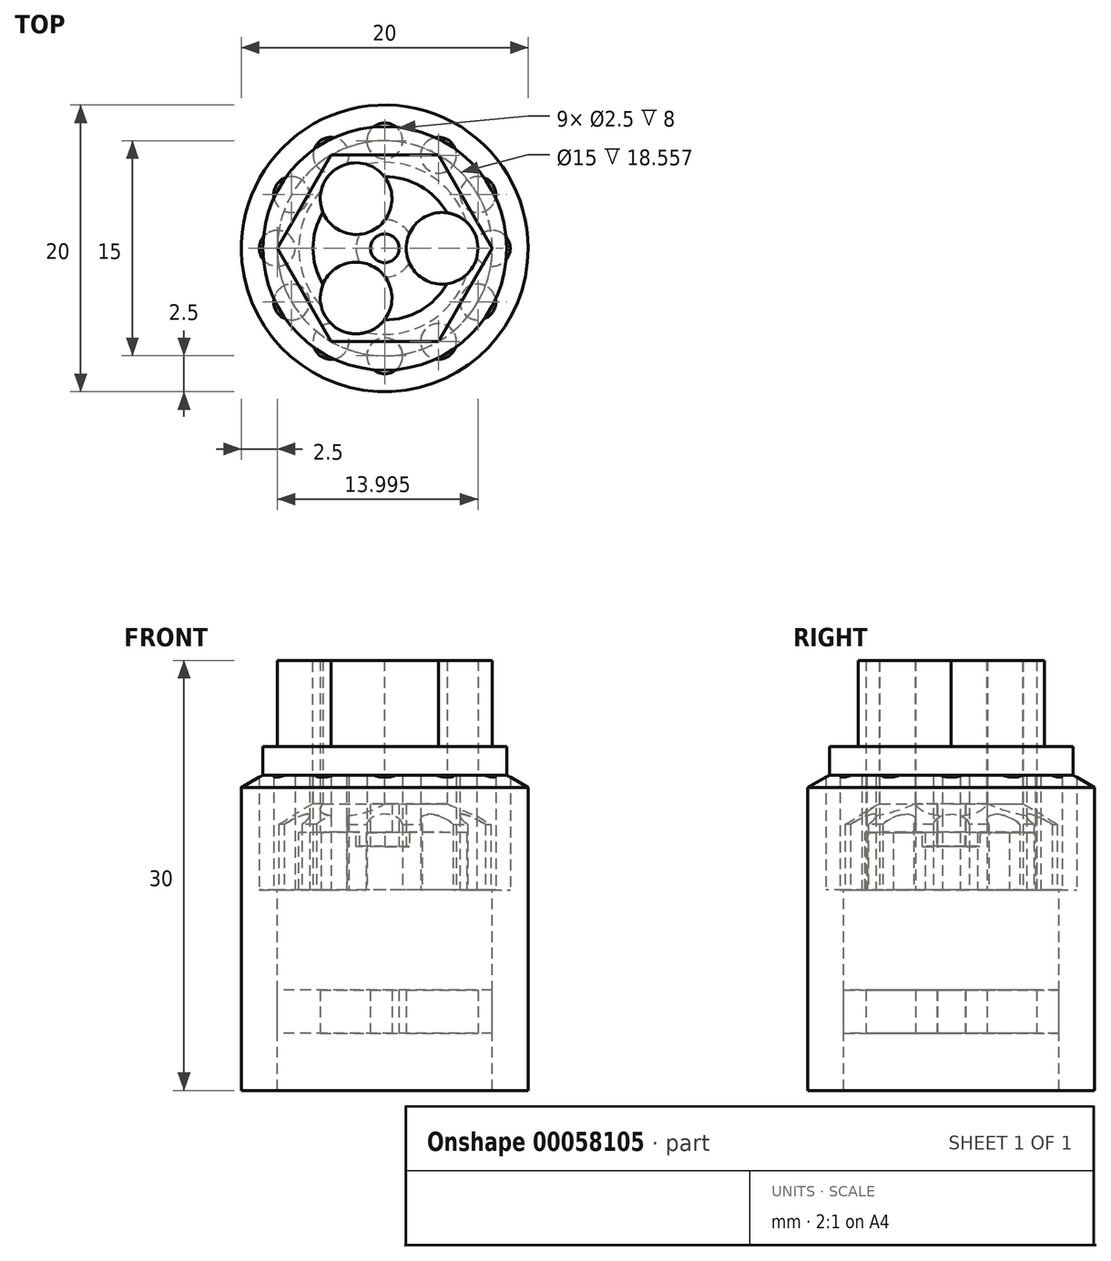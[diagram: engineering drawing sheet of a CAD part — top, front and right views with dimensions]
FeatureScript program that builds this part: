
annotation { "Feature Type Name" : "Feature", "Feature Type Description" : "" }
export const myFeature = defineFeature(function(context is Context, id is Id, definition is map)
    precondition{}
    {
        {
            var Q0;
            Q0=qCreatedBy(makeId("Front.planeOp"),FACE);
            var sketch = newSketch(context, id + "F0", { "sketchPlane" : qUnion([Q0])});
            skLineSegment(sketch, "E0", {"start": v(0, 23.15) * mm, "end": v(0, -12.35) * mm, "construction": true});
            skLineSegment(sketch, "E1", {"start": v(-5, 20) * mm, "end": v(-5, 10) * mm});
            skLineSegment(sketch, "E2", {"start": v(-5, 10) * mm, "end": v(-7.5, 8.56) * mm});
            skLineSegment(sketch, "E3", {"start": v(-7.5, 8.56) * mm, "end": v(-7.5, -10) * mm});
            skLineSegment(sketch, "E4", {"start": v(-7.5, -10) * mm, "end": v(-10, -10) * mm});
            skLineSegment(sketch, "E5", {"start": v(-10, -10) * mm, "end": v(-10, 11.13) * mm});
            skLineSegment(sketch, "E6", {"start": v(-8.5, 20) * mm, "end": v(-5, 20) * mm});
            skLineSegment(sketch, "E7.bottom", {"start": v(-7.5, -3) * mm, "end": v(0, -3) * mm});
            skLineSegment(sketch, "E7.top", {"start": v(-7.5, -6) * mm, "end": v(0, -6) * mm});
            skLineSegment(sketch, "E7.left", {"start": v(-7.5, -3) * mm, "end": v(-7.5, -6) * mm});
            skLineSegment(sketch, "E7.right", {"start": v(0, -3) * mm, "end": v(0, -6) * mm});
            skLineSegment(sketch, "E8", {"start": v(-7.5, 4) * mm, "end": v(-6, 4) * mm});
            skLineSegment(sketch, "E9", {"start": v(0, 8.03) * mm, "end": v(0, 10) * mm});
            skLineSegment(sketch, "E10", {"start": v(0, 10) * mm, "end": v(-5, 10) * mm});
            skLineSegment(sketch, "E11", {"start": v(-6, 4) * mm, "end": v(-6, 8) * mm});
            skLineSegment(sketch, "E12", {"start": v(-6, 8) * mm, "end": v(-2, 8.02) * mm});
            skLineSegment(sketch, "E13", {"start": v(-2, 8.02) * mm, "end": v(-2, 7.02) * mm});
            skLineSegment(sketch, "E14", {"start": v(-2, 7.02) * mm, "end": v(0, 7.03) * mm});
            skLineSegment(sketch, "E15", {"start": v(0, 7.03) * mm, "end": v(0, 8.03) * mm});
            skLineSegment(sketch, "E16", {"start": v(-8.5, 20) * mm, "end": v(-8.5, 12) * mm});
            skLineSegment(sketch, "E17", {"start": v(-8.5, 12) * mm, "end": v(-10, 11.13) * mm});
            skSolve(sketch);
        }
        {
            var Q0;
            Q0=makeQuery(id+"F0.imprint","IMPRINT",FACE,{"disambiguationData":[TD([[makeQuery(id+"F0.imprint","IMPRINT",EDGE,{"derivedFrom":sQuery(id+"F0.wireOp",EDGE,"E1")}),-1.0]])]});
            var Q1;
            Q1=sQuery(id+"F0.wireOp",EDGE,"E0");
            revolve(context, id + "F1", {"entities" : qUnion([Q0]), "axis" : qUnion([Q1]), "revolveType" : RevolveType.FULL});
        }
        {
            var Q0;
            {var subQ2=sQuery(id+"F0.wireOp",EDGE,"E2");Q0=makeQuery(id+"F0.imprint","IMPRINT",FACE,{"disambiguationData":[TD([[makeQuery(id+"F0.imprint","IMPRINT",EDGE,{"derivedFrom":subQ2}),1.0]])]});}
            var Q1;
            Q1=sQuery(id+"F0.wireOp",EDGE,"E0");
            revolve(context, id + "F2", {"entities" : qUnion([Q0]), "axis" : qUnion([Q1]), "revolveType" : RevolveType.FULL});
        }
        {
            var Q0;
            Q0=makeQuery(id+"F0.imprint","IMPRINT",FACE,{"disambiguationData":[TD([[makeQuery(id+"F0.imprint","IMPRINT",EDGE,{"derivedFrom":sQuery(id+"F0.wireOp",EDGE,"E7.bottom")}),-1.0]])]});
            var Q1;
            Q1=sQuery(id+"F0.wireOp",EDGE,"E0");
            revolve(context, id + "F3", {"entities" : qUnion([Q0]), "axis" : qUnion([Q1]), "revolveType" : RevolveType.FULL});
        }
        {
            var Q0;
            Q0=makeQuery(id+"F3.opRevolve","SWEPT_FACE",FACE,{"disambiguationData":[OSD([sQuery(id+"F0.wireOp",EDGE,"E7.top")])]});
            var sketch = newSketch(context, id + "F4", { "sketchPlane" : qUnion([Q0])});
            skCircle(sketch, "E18", {"center": v(4, 0) * mm, "radius": 2.5 * mm});
            skCircle(sketch, "E19.1.0", {"center": v(-2, 3.46) * mm, "radius": 2.5 * mm});
            skCircle(sketch, "E19.2.0", {"center": v(-2, -3.46) * mm, "radius": 2.5 * mm});
            skPoint(sketch, "E19.center", {"position": v(0, 0) * mm});
            skCircle(sketch, "E20", {"center": v(0, 0) * mm, "radius": 1 * mm});
            skSolve(sketch);
        }
        {
            var Q0;
            Q0 = qSketchRegion(id + "F4", true);
            extrude(context, id + "F5", {"entities" : qUnion([Q0]), "operationType" : NewBodyOperationType.REMOVE, "endBound" : BoundingType.THROUGH_ALL, "oppositeDirection" : true, "depth" : 25 * mm});
        }
        {
            var Q0;
            Q0=makeQuery(id+"F2.opRevolve","SWEPT_FACE",FACE,{"disambiguationData":[OSD([sQuery(id+"F0.wireOp",EDGE,"E8")])]});
            var sketch = newSketch(context, id + "F6", { "sketchPlane" : qUnion([Q0])});
            skCircle(sketch, "E21", {"center": v(0, 7.5) * mm, "radius": 1.25 * mm});
            skCircle(sketch, "E22.1.0", {"center": v(-3.75, 6.5) * mm, "radius": 1.25 * mm});
            skCircle(sketch, "E22.2.0", {"center": v(-6.5, 3.75) * mm, "radius": 1.25 * mm});
            skCircle(sketch, "E22.3.0", {"center": v(-7.5, 0) * mm, "radius": 1.25 * mm});
            skCircle(sketch, "E22.4.0", {"center": v(-6.5, -3.75) * mm, "radius": 1.25 * mm});
            skCircle(sketch, "E22.5.0", {"center": v(-3.75, -6.5) * mm, "radius": 1.25 * mm});
            skCircle(sketch, "E22.6.0", {"center": v(0, -7.5) * mm, "radius": 1.25 * mm});
            skCircle(sketch, "E22.7.0", {"center": v(3.75, -6.5) * mm, "radius": 1.25 * mm});
            skCircle(sketch, "E22.8.0", {"center": v(6.5, -3.75) * mm, "radius": 1.25 * mm});
            skCircle(sketch, "E22.9.0", {"center": v(7.5, 0) * mm, "radius": 1.25 * mm});
            skCircle(sketch, "E22.10.0", {"center": v(6.5, 3.75) * mm, "radius": 1.25 * mm});
            skCircle(sketch, "E22.11.0", {"center": v(3.75, 6.5) * mm, "radius": 1.25 * mm});
            skPoint(sketch, "E22.center", {"position": v(0, 0) * mm});
            skSolve(sketch);
        }
        {
            var Q0;
            Q0 = qSketchRegion(id + "F6", true);
            extrude(context, id + "F7", {"entities" : qUnion([Q0]), "operationType" : NewBodyOperationType.REMOVE, "oppositeDirection" : true, "depth" : 8 * mm});
        }
        {
            var Q0;
            Q0=makeQuery(id+"F1.opRevolve","SWEPT_FACE",FACE,{"disambiguationData":[OSD([sQuery(id+"F0.wireOp",EDGE,"E6")])]});
            var sketch = newSketch(context, id + "F8", { "sketchPlane" : qUnion([Q0])});
            skCircle(sketch, "E23.cCircle", {"center": v(0, 0) * mm, "radius": 6.5 * mm, "construction": true});
            skLineSegment(sketch, "E23.0", {"start": v(-7.5, 0) * mm, "end": v(-3.75, 6.5) * mm});
            skLineSegment(sketch, "E23.1", {"start": v(-3.75, 6.5) * mm, "end": v(3.75, 6.5) * mm});
            skLineSegment(sketch, "E23.2", {"start": v(3.75, 6.5) * mm, "end": v(7.5, 0) * mm});
            skLineSegment(sketch, "E23.3", {"start": v(7.5, 0) * mm, "end": v(3.75, -6.5) * mm});
            skLineSegment(sketch, "E23.4", {"start": v(3.75, -6.5) * mm, "end": v(-3.75, -6.5) * mm});
            skLineSegment(sketch, "E23.5", {"start": v(-3.75, -6.5) * mm, "end": v(-7.5, 0) * mm});
            skPoint(sketch, "E23.0.midPoint", {"position": v(-5.63, 3.25) * mm});
            skCircle(sketch, "E24", {"center": v(0, 0) * mm, "radius": 9 * mm});
            skSolve(sketch);
        }
        {
            var Q0;
            Q0=makeQuery(id+"F8.imprint","IMPRINT",FACE,{"disambiguationData":[TD([[makeQuery(id+"F8.imprint","IMPRINT",EDGE,{"derivedFrom":sQuery(id+"F8.wireOp",EDGE,"E23.0")}),1.0]])]});
            extrude(context, id + "F9", {"entities" : qUnion([Q0]), "operationType" : NewBodyOperationType.REMOVE, "oppositeDirection" : true, "depth" : 6 * mm});
        }
    });
